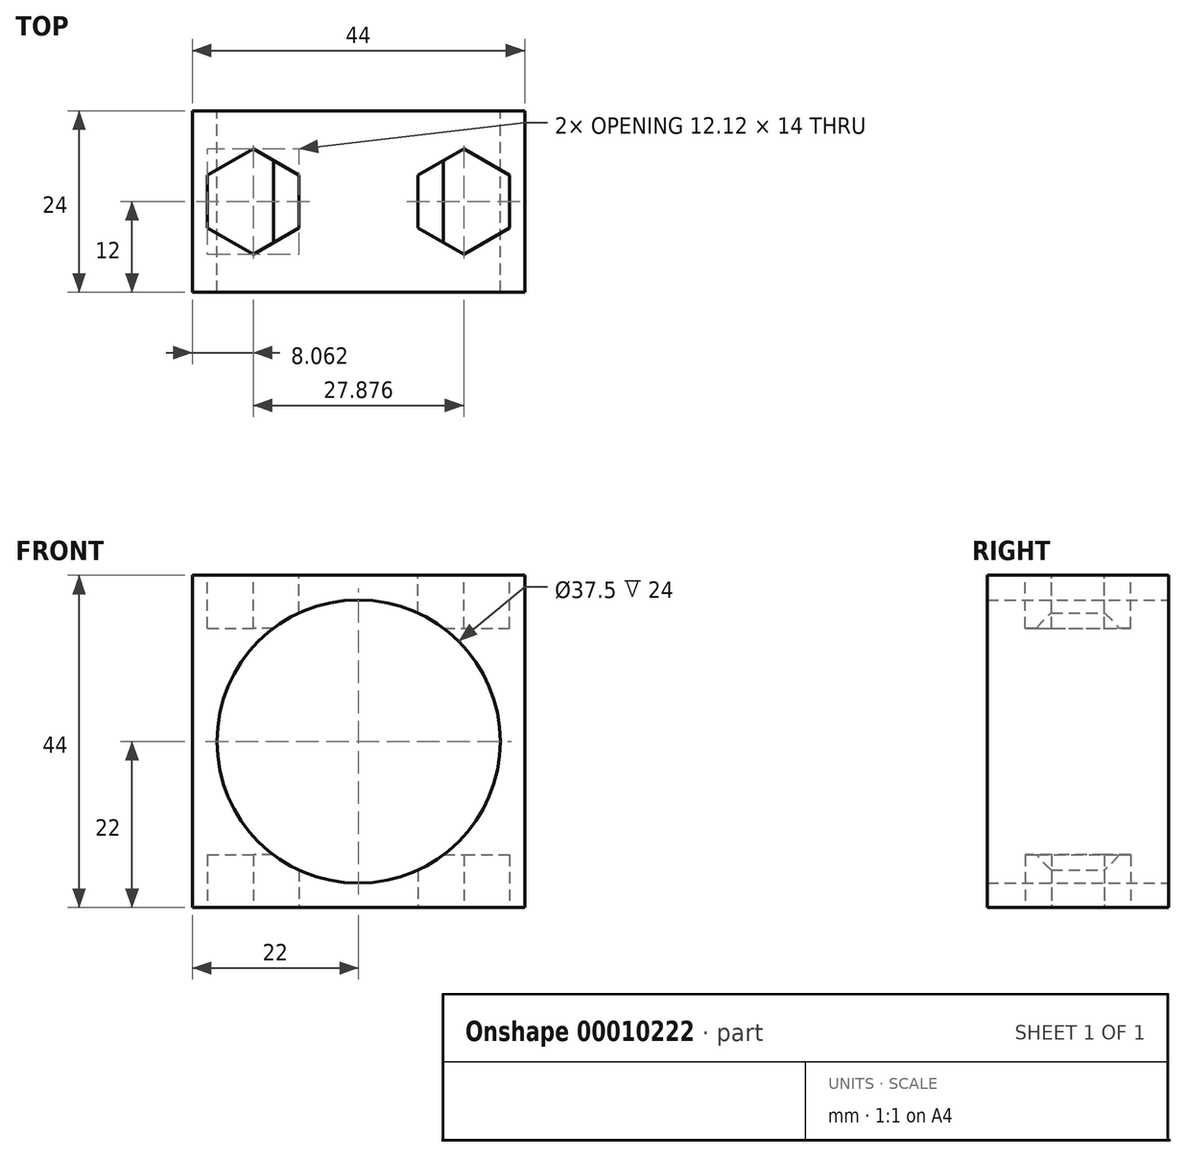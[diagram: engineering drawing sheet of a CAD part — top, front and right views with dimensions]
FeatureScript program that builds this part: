
annotation { "Feature Type Name" : "Feature", "Feature Type Description" : "" }
export const myFeature = defineFeature(function(context is Context, id is Id, definition is map)
    precondition{}
    {
        {
            var Q0;
            Q0=qCreatedBy(makeId("Front.planeOp"),FACE);
            var sketch = newSketch(context, id + "F0", { "sketchPlane" : qUnion([Q0])});
            skLineSegment(sketch, "E0.rect.bottom", {"start": v(22, -22) * mm, "end": v(-22, -22) * mm});
            skLineSegment(sketch, "E0.rect.top", {"start": v(22, 22) * mm, "end": v(-22, 22) * mm});
            skLineSegment(sketch, "E0.rect.left", {"start": v(22, -22) * mm, "end": v(22, 22) * mm});
            skLineSegment(sketch, "E0.rect.right", {"start": v(-22, -22) * mm, "end": v(-22, 22) * mm});
            skPoint(sketch, "E0.rect.middle", {"position": v(0, 0) * mm});
            skCircle(sketch, "E1", {"center": v(0, 0) * mm, "radius": 18.75 * mm});
            skSolve(sketch);
        }
        {
            var Q0;
            Q0 = qSketchRegion(id + "F0", true);
            extrude(context, id + "F1", {"entities" : qUnion([Q0]), "depth" : 24 * mm});
        }
        {
            var Q0;
            Q0=makeQuery(id+"F1.opExtrude","SWEPT_FACE",FACE,{"disambiguationData":[OSD([sQuery(id+"F0.wireOp",EDGE,"E0.rect.top")])]});
            var sketch = newSketch(context, id + "F2", { "sketchPlane" : qUnion([Q0])});
            skCircle(sketch, "E2.cCircle", {"center": v(-13.94, -12) * mm, "radius": 6.06 * mm, "construction": true});
            skLineSegment(sketch, "E2.0", {"start": v(-7.88, -15.5) * mm, "end": v(-13.94, -19) * mm});
            skLineSegment(sketch, "E2.1", {"start": v(-13.94, -19) * mm, "end": v(-20, -15.5) * mm});
            skLineSegment(sketch, "E2.2", {"start": v(-20, -15.5) * mm, "end": v(-20, -8.5) * mm});
            skLineSegment(sketch, "E2.3", {"start": v(-20, -8.5) * mm, "end": v(-13.94, -5) * mm});
            skLineSegment(sketch, "E2.4", {"start": v(-13.94, -5) * mm, "end": v(-7.88, -8.5) * mm});
            skLineSegment(sketch, "E2.5", {"start": v(-7.88, -8.5) * mm, "end": v(-7.88, -15.5) * mm});
            skPoint(sketch, "E2.0.midPoint", {"position": v(-10.9, -17.25) * mm});
            skLineSegment(sketch, "E3", {"start": v(0, 0) * mm, "end": v(0, -24) * mm, "construction": true});
            skLineSegment(sketch, "E4.0.MirrorCS", {"start": v(7.88, -15.5) * mm, "end": v(13.94, -19) * mm});
            skPoint(sketch, "E4.1.MirrorP", {"position": v(10.9, -17.25) * mm});
            skCircle(sketch, "E4.2.MirrorC", {"center": v(13.94, -12) * mm, "radius": 6.06 * mm, "construction": true});
            skLineSegment(sketch, "E4.3.MirrorCS", {"start": v(13.94, -19) * mm, "end": v(20, -15.5) * mm});
            skLineSegment(sketch, "E4.4.MirrorCS", {"start": v(20, -15.5) * mm, "end": v(20, -8.5) * mm});
            skLineSegment(sketch, "E4.5.MirrorCS", {"start": v(20, -8.5) * mm, "end": v(13.94, -5) * mm});
            skLineSegment(sketch, "E4.6.MirrorCS", {"start": v(7.88, -8.5) * mm, "end": v(7.88, -15.5) * mm});
            skLineSegment(sketch, "E4.7.MirrorCS", {"start": v(13.94, -5) * mm, "end": v(7.88, -8.5) * mm});
            skSolve(sketch);
        }
        {
            var Q0;
            Q0 = qSketchRegion(id + "F2", true);
            extrude(context, id + "F3", {"entities" : qUnion([Q0]), "operationType" : NewBodyOperationType.REMOVE, "oppositeDirection" : true, "depth" : 7 * mm});
        }
        {
            var Q0;
            Q0=makeQuery(id+"F1.opExtrude","SWEPT_FACE",FACE,{"disambiguationData":[OSD([sQuery(id+"F0.wireOp",EDGE,"E0.rect.bottom")])]});
            var sketch = newSketch(context, id + "F4", { "sketchPlane" : qUnion([Q0])});
            skCircle(sketch, "E5.cCircle", {"center": v(-13.94, 12) * mm, "radius": 6.06 * mm, "construction": true});
            skLineSegment(sketch, "E5.0", {"start": v(-7.88, 8.5) * mm, "end": v(-13.94, 5) * mm});
            skLineSegment(sketch, "E5.1", {"start": v(-13.94, 5) * mm, "end": v(-20, 8.5) * mm});
            skLineSegment(sketch, "E5.2", {"start": v(-20, 8.5) * mm, "end": v(-20, 15.5) * mm});
            skLineSegment(sketch, "E5.3", {"start": v(-20, 15.5) * mm, "end": v(-13.94, 19) * mm});
            skLineSegment(sketch, "E5.4", {"start": v(-13.94, 19) * mm, "end": v(-7.88, 15.5) * mm});
            skLineSegment(sketch, "E5.5", {"start": v(-7.88, 15.5) * mm, "end": v(-7.88, 8.5) * mm});
            skPoint(sketch, "E5.0.midPoint", {"position": v(-10.9, 6.75) * mm});
            skLineSegment(sketch, "E6", {"start": v(0, 24) * mm, "end": v(0, 0) * mm, "construction": true});
            skLineSegment(sketch, "E7.0.MirrorCS", {"start": v(7.88, 8.5) * mm, "end": v(13.94, 5) * mm});
            skLineSegment(sketch, "E7.1.MirrorCS", {"start": v(13.94, 5) * mm, "end": v(20, 8.5) * mm});
            skLineSegment(sketch, "E7.2.MirrorCS", {"start": v(20, 15.5) * mm, "end": v(13.94, 19) * mm});
            skLineSegment(sketch, "E7.3.MirrorCS", {"start": v(20, 8.5) * mm, "end": v(20, 15.5) * mm});
            skLineSegment(sketch, "E7.4.MirrorCS", {"start": v(13.94, 19) * mm, "end": v(7.88, 15.5) * mm});
            skLineSegment(sketch, "E7.5.MirrorCS", {"start": v(7.88, 15.5) * mm, "end": v(7.88, 8.5) * mm});
            skPoint(sketch, "E7.6.MirrorP", {"position": v(10.9, 6.75) * mm});
            skCircle(sketch, "E7.7.MirrorC", {"center": v(13.94, 12) * mm, "radius": 6.06 * mm, "construction": true});
            skLineSegment(sketch, "E8", {"start": v(13.94, 12) * mm, "end": v(13.94, 0) * mm, "construction": true});
            skLineSegment(sketch, "E9", {"start": v(13.94, 12) * mm, "end": v(22, 12) * mm, "construction": true});
            skSolve(sketch);
        }
        {
            var Q0;
            Q0 = qSketchRegion(id + "F4", true);
            extrude(context, id + "F5", {"entities" : qUnion([Q0]), "operationType" : NewBodyOperationType.REMOVE, "oppositeDirection" : true, "depth" : 7 * mm});
        }
    });
